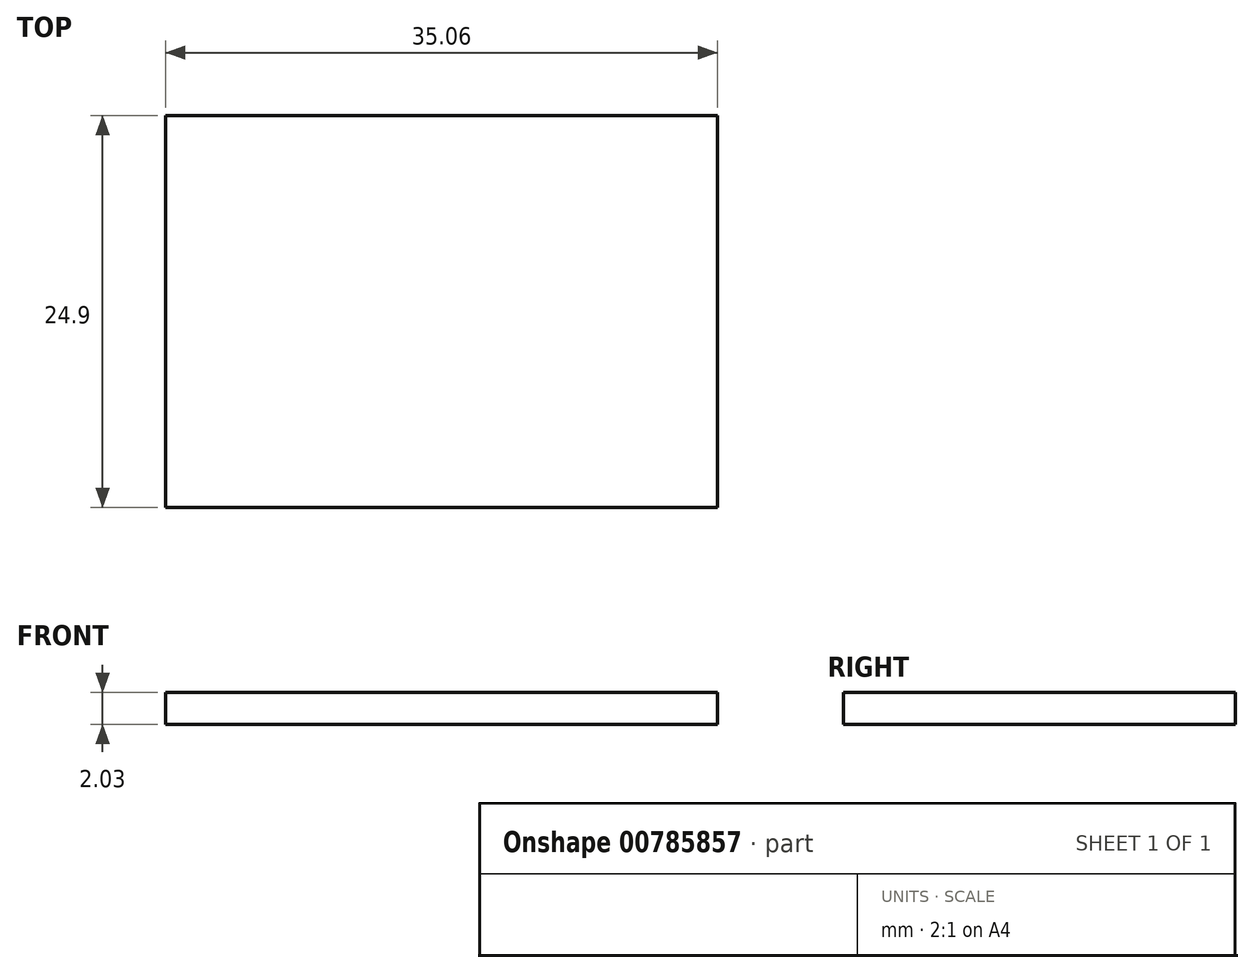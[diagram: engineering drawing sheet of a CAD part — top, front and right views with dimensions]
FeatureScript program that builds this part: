
annotation { "Feature Type Name" : "Feature", "Feature Type Description" : "" }
export const myFeature = defineFeature(function(context is Context, id is Id, definition is map)
    precondition{}
    {
        {
            var Q0;
            Q0=qCreatedBy(makeId("Top.planeOp"),FACE);
            var sketch = newSketch(context, id + "F0", { "sketchPlane" : qUnion([Q0])});
            skLineSegment(sketch, "E0.bottom", {"start": v(18.8, -18.8) * mm, "end": v(-18.8, -18.8) * mm});
            skLineSegment(sketch, "E0.top", {"start": v(18.8, 18.8) * mm, "end": v(-18.8, 18.8) * mm});
            skLineSegment(sketch, "E0.left", {"start": v(18.8, -18.8) * mm, "end": v(18.8, 18.8) * mm});
            skLineSegment(sketch, "E0.right", {"start": v(-18.8, -18.8) * mm, "end": v(-18.8, 18.8) * mm});
            skPoint(sketch, "E0.middle", {"position": v(0, 0) * mm});
            skSolve(sketch);
        }
        {
            var Q0;
            Q0=makeQuery(id+"F0.imprint","IMPRINT",FACE,{"disambiguationData":[TD([[makeQuery(id+"F0.imprint","IMPRINT",EDGE,{"derivedFrom":sQuery(id+"F0.wireOp",EDGE,"E0.bottom")}),-1.0]])]});
            extrude(context, id + "F1", {"entities" : qUnion([Q0]), "depth" : 2.03 * mm, "offsetDistance" : 25.4 * mm});
        }
        {
            var Q0;
            Q0=makeQuery(id+"F1.opExtrude","SWEPT_FACE",FACE,{"disambiguationData":[OSD([sQuery(id+"F0.wireOp",EDGE,"E0.bottom")])]});
            var Q1;
            Q1=makeQuery(id+"F1.opExtrude","SWEPT_FACE",FACE,{"disambiguationData":[OSD([sQuery(id+"F0.wireOp",EDGE,"E0.top")])]});
            extrude(context, id + "F2", {"entities" : qUnion([Q0, Q1]), "operationType" : NewBodyOperationType.REMOVE, "endBound" : BoundingType.SYMMETRIC, "oppositeDirection" : true, "depth" : 2.54 * mm, "offsetDistance" : 25.4 * mm});
        }
        {
            var Q0;
            Q0=makeQuery(id+"F1.opExtrude","SWEPT_FACE",FACE,{"disambiguationData":[OSD([sQuery(id+"F0.wireOp",EDGE,"E0.left")])]});
            var Q1;
            Q1=makeQuery(id+"F1.opExtrude","SWEPT_FACE",FACE,{"disambiguationData":[OSD([sQuery(id+"F0.wireOp",EDGE,"E0.right")])]});
            extrude(context, id + "F3", {"entities" : qUnion([Q0, Q1]), "operationType" : NewBodyOperationType.REMOVE, "endBound" : BoundingType.SYMMETRIC, "depth" : 2.54 * mm, "offsetDistance" : 25.4 * mm});
        }
        {
            var Q0;
            Q0=makeQuery(id+"F2.boolean.opBoolean","COPY",FACE,{"derivedFrom":makeQuery(id+"F2.opExtrude","CAP_FACE",FACE,{"disambiguationData":[OSD([sQuery(id+"F0.wireOp",EDGE,"E0.bottom")])],"isStart":false})});
            extrude(context, id + "F4", {"entities" : qUnion([Q0]), "operationType" : NewBodyOperationType.REMOVE, "oppositeDirection" : true, "depth" : 10.16 * mm, "offsetDistance" : 25.4 * mm});
        }
    });
